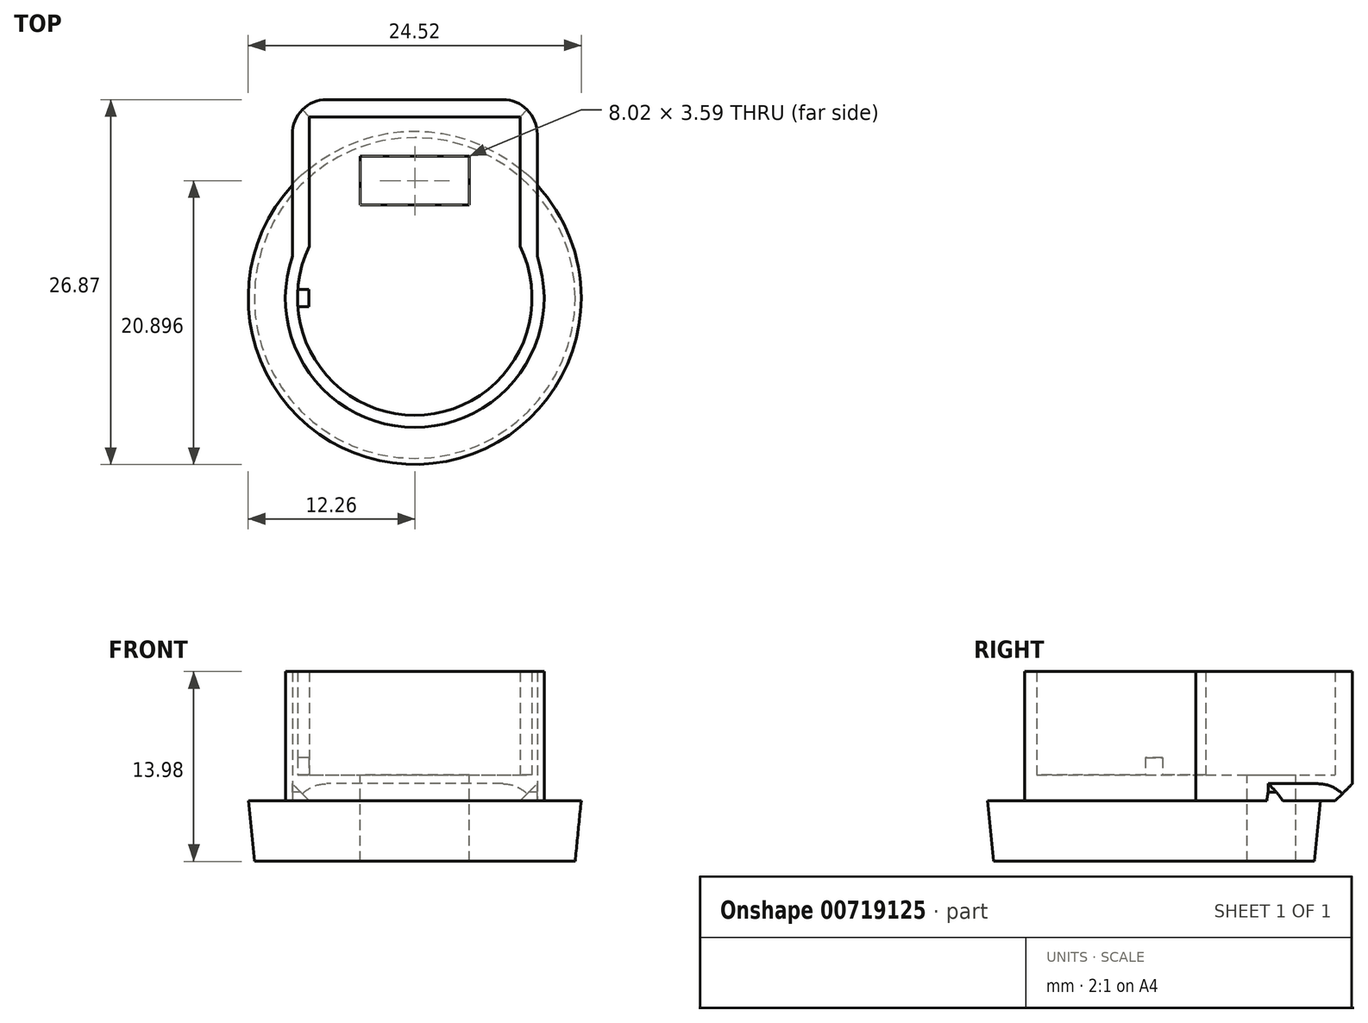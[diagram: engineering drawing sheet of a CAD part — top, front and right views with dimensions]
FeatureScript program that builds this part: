
annotation { "Feature Type Name" : "Feature", "Feature Type Description" : "" }
export const myFeature = defineFeature(function(context is Context, id is Id, definition is map)
    precondition{}
    {
        {
            var Q0;
            Q0=qCreatedBy(makeId("Top.planeOp"),FACE);
            var sketch = newSketch(context, id + "F0", { "sketchPlane" : qUnion([Q0])});
            skCircle(sketch, "E0", {"center": v(0, 0) * mm, "radius": 12.32 * mm});
            skCircle(sketch, "E1", {"center": v(0, 0) * mm, "radius": 8.64 * mm});
            skLineSegment(sketch, "E2", {"start": v(0, 8.64) * mm, "end": v(0, 13.34) * mm});
            skLineSegment(sketch, "E3", {"start": v(0, 13.34) * mm, "end": v(-7.75, 13.34) * mm});
            skLineSegment(sketch, "E4", {"start": v(-7.75, 13.34) * mm, "end": v(-7.75, 3.82) * mm});
            skLineSegment(sketch, "E5", {"start": v(0, 13.34) * mm, "end": v(7.75, 13.34) * mm});
            skLineSegment(sketch, "E6", {"start": v(7.75, 13.34) * mm, "end": v(7.75, 3.82) * mm});
            skCircle(sketch, "E7", {"center": v(0, 0) * mm, "radius": 9.53 * mm});
            skLineSegment(sketch, "E8", {"start": v(0, 13.34) * mm, "end": v(0, 14.6) * mm});
            skLineSegment(sketch, "E9", {"start": v(0, 14.6) * mm, "end": v(9.02, 14.6) * mm});
            skLineSegment(sketch, "E10", {"start": v(9.02, 14.6) * mm, "end": v(9.02, 3.07) * mm});
            skLineSegment(sketch, "E11", {"start": v(0, 14.6) * mm, "end": v(-9.02, 14.6) * mm});
            skLineSegment(sketch, "E12", {"start": v(-9.02, 14.6) * mm, "end": v(-9.02, 3.07) * mm});
            skLineSegment(sketch, "E13.bottom", {"start": v(4, 6.84) * mm, "end": v(-4, 6.84) * mm});
            skLineSegment(sketch, "E13.top", {"start": v(4, 10.43) * mm, "end": v(-4, 10.43) * mm});
            skLineSegment(sketch, "E13.left", {"start": v(4, 6.84) * mm, "end": v(4, 10.43) * mm});
            skLineSegment(sketch, "E13.right", {"start": v(-4, 6.84) * mm, "end": v(-4, 10.43) * mm});
            skPoint(sketch, "E13.middle", {"position": v(0, 8.64) * mm});
            skSolve(sketch);
        }
        {
            var Q0;
            {var subQ0=sQuery(id+"F0.wireOp",EDGE,"E10");var subQ1=sQuery(id+"F0.wireOp",EDGE,"E0");var subQ2=makeQuery(id+"F0.imprint","INTERSECT",VERTEX,{"derivedFrom":[subQ1,subQ0]});Q0=makeQuery(id+"F0.imprint","IMPRINT",FACE,{"disambiguationData":[TD([[makeQuery(id+"F0.imprint","IMPRINT",EDGE,{"disambiguationData":[TD([[subQ2,1.0]])],"derivedFrom":subQ1}),1.0]])]});}
            var Q1;
            {var subQ0=sQuery(id+"F0.wireOp",EDGE,"E13.bottom");Q1=makeQuery(id+"F0.imprint","IMPRINT",FACE,{"disambiguationData":[TD([[makeQuery(id+"F0.imprint","IMPRINT",EDGE,{"derivedFrom":subQ0}),1.0]])]});}
            var Q2;
            {var subQ0=sQuery(id+"F0.wireOp",EDGE,"E4");var subQ1=sQuery(id+"F0.wireOp",EDGE,"E1");var subQ2=makeQuery(id+"F0.imprint","INTERSECT",VERTEX,{"derivedFrom":[subQ1,subQ0]});Q2=makeQuery(id+"F0.imprint","IMPRINT",FACE,{"disambiguationData":[TD([[makeQuery(id+"F0.imprint","IMPRINT",EDGE,{"disambiguationData":[TD([[subQ2,1.0]])],"derivedFrom":subQ1}),-1.0]])]});}
            var Q3;
            {var subQ5=sQuery(id+"F0.wireOp",EDGE,"E0");var subQ9=sQuery(id+"F0.wireOp",EDGE,"E2");var subQ11=makeQuery(id+"F0.imprint","INTERSECT",VERTEX,{"derivedFrom":[subQ5,subQ9]});Q3=makeQuery(id+"F0.imprint","IMPRINT",FACE,{"disambiguationData":[TD([[makeQuery(id+"F0.imprint","IMPRINT",EDGE,{"disambiguationData":[TD([[subQ11,-1.0]])],"derivedFrom":subQ5}),1.0]])]});}
            var Q4;
            {var subQ1=sQuery(id+"F0.wireOp",EDGE,"E6");var subQ6=sQuery(id+"F0.wireOp",EDGE,"E0");var subQ10=makeQuery(id+"F0.imprint","INTERSECT",VERTEX,{"derivedFrom":[subQ6,subQ1]});Q4=makeQuery(id+"F0.imprint","IMPRINT",FACE,{"disambiguationData":[TD([[makeQuery(id+"F0.imprint","IMPRINT",EDGE,{"disambiguationData":[TD([[subQ10,-1.0]])],"derivedFrom":subQ6}),1.0]])]});}
            var Q5;
            {var subQ0=sQuery(id+"F0.wireOp",EDGE,"E10");var subQ1=sQuery(id+"F0.wireOp",EDGE,"E0");var subQ2=makeQuery(id+"F0.imprint","INTERSECT",VERTEX,{"derivedFrom":[subQ1,subQ0]});Q5=makeQuery(id+"F0.imprint","IMPRINT",FACE,{"disambiguationData":[TD([[makeQuery(id+"F0.imprint","IMPRINT",EDGE,{"disambiguationData":[TD([[subQ2,-1.0]])],"derivedFrom":subQ1}),1.0]])]});}
            var Q6;
            {var subQ0=sQuery(id+"F0.wireOp",EDGE,"E12");var subQ1=sQuery(id+"F0.wireOp",EDGE,"E0");var subQ2=makeQuery(id+"F0.imprint","INTERSECT",VERTEX,{"derivedFrom":[subQ1,subQ0]});Q6=makeQuery(id+"F0.imprint","IMPRINT",FACE,{"disambiguationData":[TD([[makeQuery(id+"F0.imprint","IMPRINT",EDGE,{"disambiguationData":[TD([[subQ2,1.0]])],"derivedFrom":subQ1}),1.0]])]});}
            var Q7;
            {var subQ1=sQuery(id+"F0.wireOp",EDGE,"E1");var subQ6=sQuery(id+"F0.wireOp",EDGE,"E4");var subQ7=makeQuery(id+"F0.imprint","INTERSECT",VERTEX,{"derivedFrom":[subQ1,subQ6]});Q7=makeQuery(id+"F0.imprint","IMPRINT",FACE,{"disambiguationData":[TD([[makeQuery(id+"F0.imprint","IMPRINT",EDGE,{"disambiguationData":[TD([[subQ7,-1.0]])],"derivedFrom":subQ1}),-1.0]])]});}
            var Q8;
            {var subQ0=sQuery(id+"F0.wireOp",EDGE,"E6");var subQ1=sQuery(id+"F0.wireOp",EDGE,"E1");var subQ2=makeQuery(id+"F0.imprint","INTERSECT",VERTEX,{"derivedFrom":[subQ1,subQ0]});Q8=makeQuery(id+"F0.imprint","IMPRINT",FACE,{"disambiguationData":[TD([[makeQuery(id+"F0.imprint","IMPRINT",EDGE,{"disambiguationData":[TD([[subQ2,-1.0]])],"derivedFrom":subQ1}),-1.0]])]});}
            extrude(context, id + "F1", {"entities" : qUnion([Q0, Q1, Q2, Q3, Q4, Q5, Q6, Q7, Q8]), "oppositeDirection" : true, "depth" : 4.44 * mm, "offsetDistance" : 25.4 * mm});
        }
        {
            var Q0;
            {var subQ5=sQuery(id+"F0.wireOp",EDGE,"E0");var subQ9=sQuery(id+"F0.wireOp",EDGE,"E2");var subQ11=makeQuery(id+"F0.imprint","INTERSECT",VERTEX,{"derivedFrom":[subQ5,subQ9]});Q0=makeQuery(id+"F0.imprint","IMPRINT",FACE,{"disambiguationData":[TD([[makeQuery(id+"F0.imprint","IMPRINT",EDGE,{"disambiguationData":[TD([[subQ11,-1.0]])],"derivedFrom":subQ5}),1.0]])]});}
            var Q1;
            {var subQ5=sQuery(id+"F0.wireOp",EDGE,"E3");Q1=makeQuery(id+"F0.imprint","IMPRINT",FACE,{"disambiguationData":[TD([[makeQuery(id+"F0.imprint","IMPRINT",EDGE,{"derivedFrom":subQ5}),1.0]])]});}
            var Q2;
            {var subQ5=sQuery(id+"F0.wireOp",EDGE,"E5");Q2=makeQuery(id+"F0.imprint","IMPRINT",FACE,{"disambiguationData":[TD([[makeQuery(id+"F0.imprint","IMPRINT",EDGE,{"derivedFrom":subQ5}),-1.0]])]});}
            var Q3;
            {var subQ1=sQuery(id+"F0.wireOp",EDGE,"E6");var subQ6=sQuery(id+"F0.wireOp",EDGE,"E0");var subQ10=makeQuery(id+"F0.imprint","INTERSECT",VERTEX,{"derivedFrom":[subQ6,subQ1]});Q3=makeQuery(id+"F0.imprint","IMPRINT",FACE,{"disambiguationData":[TD([[makeQuery(id+"F0.imprint","IMPRINT",EDGE,{"disambiguationData":[TD([[subQ10,-1.0]])],"derivedFrom":subQ6}),1.0]])]});}
            var Q4;
            {var subQ0=sQuery(id+"F0.wireOp",EDGE,"E5");Q4=makeQuery(id+"F0.imprint","IMPRINT",FACE,{"disambiguationData":[TD([[makeQuery(id+"F0.imprint","IMPRINT",EDGE,{"derivedFrom":subQ0}),1.0]])]});}
            var Q5;
            {var subQ1=sQuery(id+"F0.wireOp",EDGE,"E3");Q5=makeQuery(id+"F0.imprint","IMPRINT",FACE,{"disambiguationData":[TD([[makeQuery(id+"F0.imprint","IMPRINT",EDGE,{"derivedFrom":subQ1}),-1.0]])]});}
            var Q6;
            {var subQ0=sQuery(id+"F0.wireOp",EDGE,"E13.bottom");Q6=makeQuery(id+"F0.imprint","IMPRINT",FACE,{"disambiguationData":[TD([[makeQuery(id+"F0.imprint","IMPRINT",EDGE,{"derivedFrom":subQ0}),1.0]])]});}
            var Q7;
            {var subQ0=sQuery(id+"F0.wireOp",EDGE,"E12");var subQ1=sQuery(id+"F0.wireOp",EDGE,"E0");var subQ2=makeQuery(id+"F0.imprint","INTERSECT",VERTEX,{"derivedFrom":[subQ1,subQ0]});Q7=makeQuery(id+"F0.imprint","IMPRINT",FACE,{"disambiguationData":[TD([[makeQuery(id+"F0.imprint","IMPRINT",EDGE,{"disambiguationData":[TD([[subQ2,1.0]])],"derivedFrom":subQ1}),1.0]])]});}
            var Q8;
            {var subQ1=sQuery(id+"F0.wireOp",EDGE,"E1");var subQ6=sQuery(id+"F0.wireOp",EDGE,"E4");var subQ7=makeQuery(id+"F0.imprint","INTERSECT",VERTEX,{"derivedFrom":[subQ1,subQ6]});Q8=makeQuery(id+"F0.imprint","IMPRINT",FACE,{"disambiguationData":[TD([[makeQuery(id+"F0.imprint","IMPRINT",EDGE,{"disambiguationData":[TD([[subQ7,-1.0]])],"derivedFrom":subQ1}),-1.0]])]});}
            var Q9;
            {var subQ0=sQuery(id+"F0.wireOp",EDGE,"E4");var subQ1=sQuery(id+"F0.wireOp",EDGE,"E1");var subQ2=makeQuery(id+"F0.imprint","INTERSECT",VERTEX,{"derivedFrom":[subQ1,subQ0]});Q9=makeQuery(id+"F0.imprint","IMPRINT",FACE,{"disambiguationData":[TD([[makeQuery(id+"F0.imprint","IMPRINT",EDGE,{"disambiguationData":[TD([[subQ2,1.0]])],"derivedFrom":subQ1}),-1.0]])]});}
            var Q10;
            {var subQ0=sQuery(id+"F0.wireOp",EDGE,"E6");var subQ1=sQuery(id+"F0.wireOp",EDGE,"E1");var subQ2=makeQuery(id+"F0.imprint","INTERSECT",VERTEX,{"derivedFrom":[subQ1,subQ0]});Q10=makeQuery(id+"F0.imprint","IMPRINT",FACE,{"disambiguationData":[TD([[makeQuery(id+"F0.imprint","IMPRINT",EDGE,{"disambiguationData":[TD([[subQ2,-1.0]])],"derivedFrom":subQ1}),-1.0]])]});}
            var Q11;
            {var subQ0=sQuery(id+"F0.wireOp",EDGE,"E10");var subQ1=sQuery(id+"F0.wireOp",EDGE,"E0");var subQ2=makeQuery(id+"F0.imprint","INTERSECT",VERTEX,{"derivedFrom":[subQ1,subQ0]});Q11=makeQuery(id+"F0.imprint","IMPRINT",FACE,{"disambiguationData":[TD([[makeQuery(id+"F0.imprint","IMPRINT",EDGE,{"disambiguationData":[TD([[subQ2,-1.0]])],"derivedFrom":subQ1}),1.0]])]});}
            extrude(context, id + "F2", {"entities" : qUnion([Q0, Q1, Q2, Q3, Q4, Q5, Q6, Q7, Q8, Q9, Q10, Q11]), "operationType" : NewBodyOperationType.ADD, "depth" : 1.9 * mm, "offsetDistance" : 25.4 * mm});
        }
        {
            var Q0;
            {var subQ1=sQuery(id+"F0.wireOp",EDGE,"E3");Q0=makeQuery(id+"F0.imprint","IMPRINT",FACE,{"disambiguationData":[TD([[makeQuery(id+"F0.imprint","IMPRINT",EDGE,{"derivedFrom":subQ1}),-1.0]])]});}
            var Q1;
            {var subQ0=sQuery(id+"F0.wireOp",EDGE,"E5");Q1=makeQuery(id+"F0.imprint","IMPRINT",FACE,{"disambiguationData":[TD([[makeQuery(id+"F0.imprint","IMPRINT",EDGE,{"derivedFrom":subQ0}),1.0]])]});}
            var Q2;
            {var subQ0=sQuery(id+"F0.wireOp",EDGE,"E10");var subQ1=sQuery(id+"F0.wireOp",EDGE,"E0");var subQ2=makeQuery(id+"F0.imprint","INTERSECT",VERTEX,{"derivedFrom":[subQ1,subQ0]});Q2=makeQuery(id+"F0.imprint","IMPRINT",FACE,{"disambiguationData":[TD([[makeQuery(id+"F0.imprint","IMPRINT",EDGE,{"disambiguationData":[TD([[subQ2,-1.0]])],"derivedFrom":subQ1}),1.0]])]});}
            var Q3;
            {var subQ1=sQuery(id+"F0.wireOp",EDGE,"E1");var subQ6=sQuery(id+"F0.wireOp",EDGE,"E4");var subQ7=makeQuery(id+"F0.imprint","INTERSECT",VERTEX,{"derivedFrom":[subQ1,subQ6]});Q3=makeQuery(id+"F0.imprint","IMPRINT",FACE,{"disambiguationData":[TD([[makeQuery(id+"F0.imprint","IMPRINT",EDGE,{"disambiguationData":[TD([[subQ7,-1.0]])],"derivedFrom":subQ1}),-1.0]])]});}
            var Q4;
            {var subQ0=sQuery(id+"F0.wireOp",EDGE,"E12");var subQ1=sQuery(id+"F0.wireOp",EDGE,"E0");var subQ2=makeQuery(id+"F0.imprint","INTERSECT",VERTEX,{"derivedFrom":[subQ1,subQ0]});Q4=makeQuery(id+"F0.imprint","IMPRINT",FACE,{"disambiguationData":[TD([[makeQuery(id+"F0.imprint","IMPRINT",EDGE,{"disambiguationData":[TD([[subQ2,1.0]])],"derivedFrom":subQ1}),1.0]])]});}
            extrude(context, id + "F3", {"entities" : qUnion([Q0, Q1, Q2, Q3, Q4]), "operationType" : NewBodyOperationType.ADD, "depth" : 9.52 * mm, "offsetDistance" : 25.4 * mm});
        }
        {
            var Q0;
            Q0=makeQuery(id+"F2.opExtrude","CAP_FACE",FACE,{"disambiguationData":[OSD([sQuery(id+"F0.wireOp",EDGE,"E7"),sQuery(id+"F0.wireOp",EDGE,"E9"),sQuery(id+"F0.wireOp",EDGE,"E10"),sQuery(id+"F0.wireOp",EDGE,"E11"),sQuery(id+"F0.wireOp",EDGE,"E12"),sQuery(id+"F0.wireOp",EDGE,"E13.bottom"),sQuery(id+"F0.wireOp",EDGE,"E13.top"),sQuery(id+"F0.wireOp",EDGE,"E13.left"),sQuery(id+"F0.wireOp",EDGE,"E13.right")])],"isStart":false});
            var sketch = newSketch(context, id + "F4", { "sketchPlane" : qUnion([Q0])});
            skLineSegment(sketch, "E14.bottom", {"start": v(-7.81, -0.64) * mm, "end": v(-9.46, -0.63) * mm});
            skLineSegment(sketch, "E14.top", {"start": v(-7.81, 0.64) * mm, "end": v(-9.46, 0.64) * mm});
            skLineSegment(sketch, "E14.left", {"start": v(-7.81, -0.64) * mm, "end": v(-7.81, 0.64) * mm});
            skLineSegment(sketch, "E14.right", {"start": v(-9.46, -0.63) * mm, "end": v(-9.46, 0.64) * mm});
            skPoint(sketch, "E14.middle", {"position": v(-8.64, 0) * mm});
            skSolve(sketch);
        }
        {
            var Q0;
            {var subQ0=sQuery(id+"F4.wireOp",EDGE,"E14.left");Q0=makeQuery(id+"F4.imprint","IMPRINT",FACE,{"disambiguationData":[TD([[makeQuery(id+"F4.imprint","IMPRINT",EDGE,{"derivedFrom":subQ0}),1.0]])]});}
            extrude(context, id + "F5", {"entities" : qUnion([Q0]), "operationType" : NewBodyOperationType.ADD, "depth" : 1.27 * mm, "offsetDistance" : 25.4 * mm});
        }
        {
            var Q0;
            Q0=makeQuery(id+"F2.opExtrude","CAP_EDGE",EDGE,{"disambiguationData":[OSD([sQuery(id+"F0.wireOp",EDGE,"E9"),sQuery(id+"F0.wireOp",EDGE,"E11")])],"isStart":true});
            var Q1;
            {var subQ0=sQuery(id+"F0.wireOp",EDGE,"E12");Q1=makeQuery(id+"F2.boolean.opBoolean","SPLIT",EDGE,{"disambiguationData":[topologyDisambiguationEdgeConnected([makeQuery(id+"F2.opExtrude","CAP_FACE",FACE,{"disambiguationData":[OSD([sQuery(id+"F0.wireOp",EDGE,"E7"),sQuery(id+"F0.wireOp",EDGE,"E9"),sQuery(id+"F0.wireOp",EDGE,"E10"),sQuery(id+"F0.wireOp",EDGE,"E11"),subQ0,sQuery(id+"F0.wireOp",EDGE,"E13.bottom"),sQuery(id+"F0.wireOp",EDGE,"E13.top"),sQuery(id+"F0.wireOp",EDGE,"E13.left"),sQuery(id+"F0.wireOp",EDGE,"E13.right")])],"isStart":true})])],"derivedFrom":makeQuery(id+"F2.opExtrude","CAP_EDGE",EDGE,{"disambiguationData":[OSD([subQ0])],"isStart":true})});}
            var Q2;
            {var subQ0=sQuery(id+"F0.wireOp",EDGE,"E10");Q2=makeQuery(id+"F2.boolean.opBoolean","SPLIT",EDGE,{"disambiguationData":[topologyDisambiguationEdgeConnected([makeQuery(id+"F2.opExtrude","CAP_FACE",FACE,{"disambiguationData":[OSD([sQuery(id+"F0.wireOp",EDGE,"E7"),sQuery(id+"F0.wireOp",EDGE,"E9"),subQ0,sQuery(id+"F0.wireOp",EDGE,"E11"),sQuery(id+"F0.wireOp",EDGE,"E12"),sQuery(id+"F0.wireOp",EDGE,"E13.bottom"),sQuery(id+"F0.wireOp",EDGE,"E13.top"),sQuery(id+"F0.wireOp",EDGE,"E13.left"),sQuery(id+"F0.wireOp",EDGE,"E13.right")])],"isStart":true})])],"derivedFrom":makeQuery(id+"F2.opExtrude","CAP_EDGE",EDGE,{"disambiguationData":[OSD([subQ0])],"isStart":true})});}
            chamfer(context, id + "F6", {"entities" : qUnion([Q0, Q1, Q2]), "width" : 1.27 * mm, "tangentPropagation" : true});
        }
        {
            var Q0;
            {var subQ0=sQuery(id+"F0.wireOp",EDGE,"E12");var subQ1=sQuery(id+"F0.wireOp",EDGE,"E11");Q0=makeQuery(id+"F3.boolean.opBoolean","MERGE",EDGE,{"derivedFrom":[makeQuery(id+"F2.opExtrude","SWEPT_EDGE",EDGE,{"disambiguationData":[OSD([subQ1,subQ0])]}),makeQuery(id+"F3.opExtrude","SWEPT_EDGE",EDGE,{"disambiguationData":[OSD([subQ1,subQ0])]})]});}
            var Q1;
            {var subQ0=sQuery(id+"F0.wireOp",EDGE,"E10");var subQ1=sQuery(id+"F0.wireOp",EDGE,"E9");Q1=makeQuery(id+"F3.boolean.opBoolean","MERGE",EDGE,{"derivedFrom":[makeQuery(id+"F2.opExtrude","SWEPT_EDGE",EDGE,{"disambiguationData":[OSD([subQ1,subQ0])]}),makeQuery(id+"F3.opExtrude","SWEPT_EDGE",EDGE,{"disambiguationData":[OSD([subQ1,subQ0])]})]});}
            fillet(context, id + "F7", {"entities" : qUnion([Q0, Q1]), "radius" : 2.54 * mm, "tangentPropagation" : true, "allowEdgeOverflow" : false});
        }
        {
            var Q0;
            Q0=makeQuery(id+"F1.opExtrude","CAP_EDGE",EDGE,{"disambiguationData":[OSD([sQuery(id+"F0.wireOp",EDGE,"E0")])],"isStart":false});
            chamfer(context, id + "F8", {"entities" : qUnion([Q0]), "chamferType" : ChamferType.TWO_OFFSETS, "width1" : 5.08 * mm, "oppositeDirection" : false, "width2" : 0.5 * mm, "tangentPropagation" : true});
        }
    });
